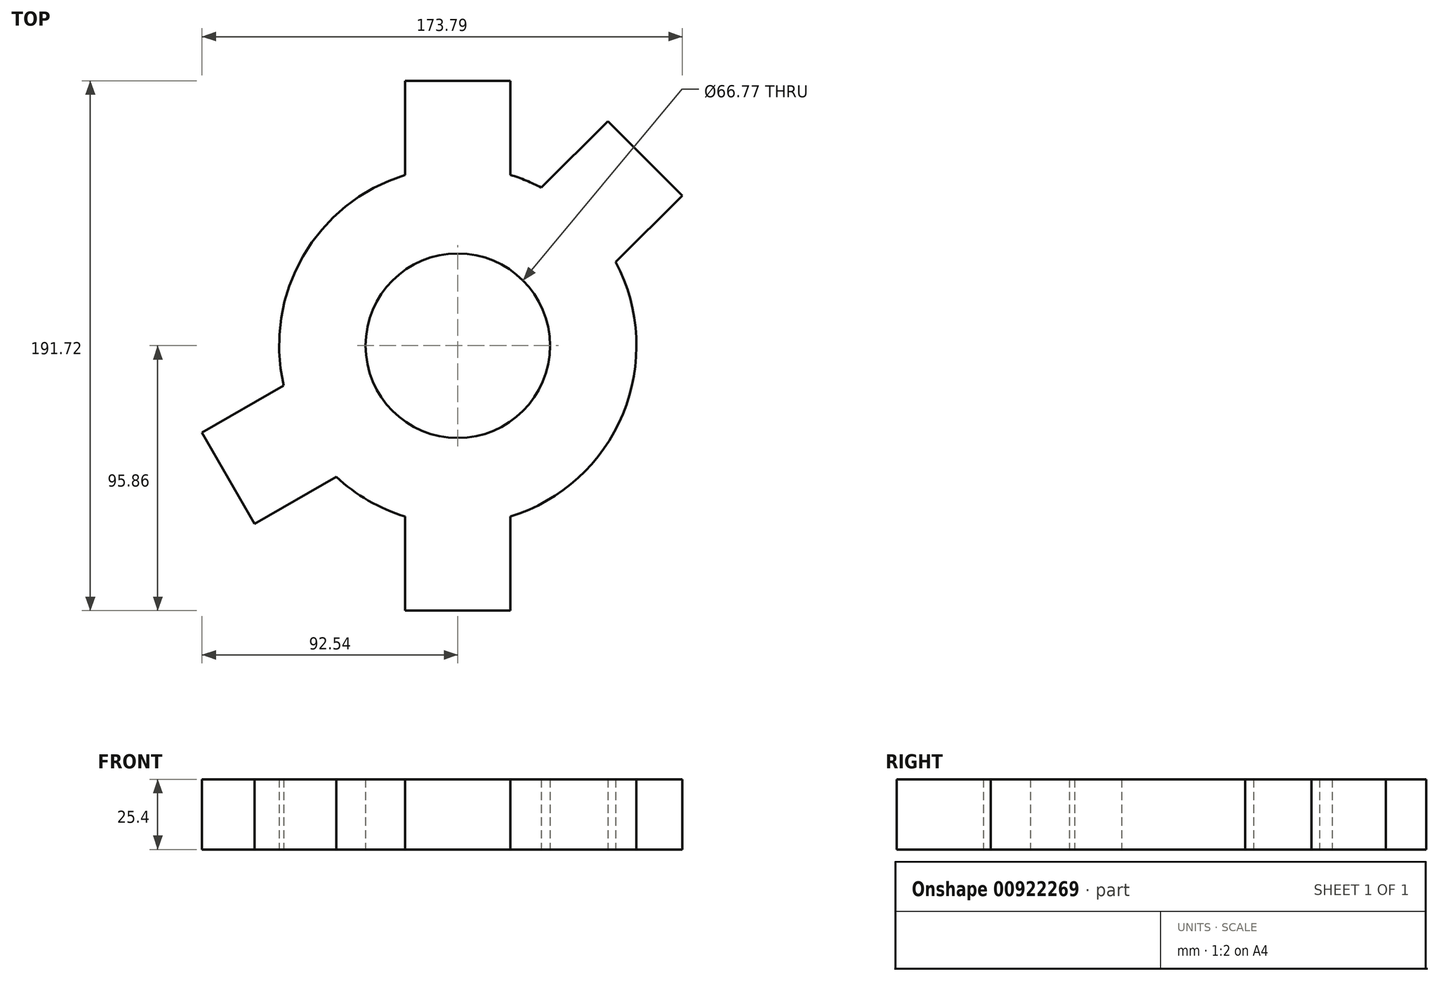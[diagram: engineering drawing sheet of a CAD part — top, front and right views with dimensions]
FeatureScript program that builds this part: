
annotation { "Feature Type Name" : "Feature", "Feature Type Description" : "" }
export const myFeature = defineFeature(function(context is Context, id is Id, definition is map)
    precondition{}
    {
        {
            var Q0;
            Q0=qCreatedBy(makeId("Top.planeOp"),FACE);
            var sketch = newSketch(context, id + "F0", { "sketchPlane" : qUnion([Q0])});
            skCircle(sketch, "E0", {"center": v(0, 0) * mm, "radius": 64.69 * mm});
            skCircle(sketch, "E1", {"center": v(0, 0) * mm, "radius": 33.38 * mm});
            skLineSegment(sketch, "E2", {"start": v(0, 0) * mm, "end": v(0, -64.69) * mm, "construction": true});
            skLineSegment(sketch, "E3", {"start": v(0, 0) * mm, "end": v(45.74, 45.74) * mm, "construction": true});
            skLineSegment(sketch, "E4", {"start": v(0, 0) * mm, "end": v(0, 64.69) * mm, "construction": true});
            skLineSegment(sketch, "E5", {"start": v(0, 0) * mm, "end": v(-56.02, -32.34) * mm, "construction": true});
            skLineSegment(sketch, "E6", {"start": v(19.05, -61.82) * mm, "end": v(19.05, -95.86) * mm});
            skLineSegment(sketch, "E7", {"start": v(30.24, 57.18) * mm, "end": v(54.3, 81.25) * mm});
            skLineSegment(sketch, "E8", {"start": v(19.05, 61.82) * mm, "end": v(19.05, 95.86) * mm});
            skLineSegment(sketch, "E9", {"start": v(-63.06, -14.41) * mm, "end": v(-92.54, -31.43) * mm});
            skLineSegment(sketch, "E10", {"start": v(19.05, -95.86) * mm, "end": v(0, -95.86) * mm});
            skLineSegment(sketch, "E11", {"start": v(54.3, 81.25) * mm, "end": v(67.78, 67.78) * mm});
            skLineSegment(sketch, "E12", {"start": v(19.05, 95.86) * mm, "end": v(0, 95.86) * mm});
            skLineSegment(sketch, "E13", {"start": v(-92.54, -31.43) * mm, "end": v(-83.01, -47.93) * mm});
            skLineSegment(sketch, "E14.MirrorCS", {"start": v(-19.05, -61.82) * mm, "end": v(-19.05, -95.86) * mm});
            skLineSegment(sketch, "E15.MirrorCS", {"start": v(-19.05, -95.86) * mm, "end": v(0, -95.86) * mm});
            skLineSegment(sketch, "E16.MirrorCS", {"start": v(-19.05, 61.82) * mm, "end": v(-19.05, 95.86) * mm});
            skLineSegment(sketch, "E17.MirrorCS", {"start": v(-19.05, 95.86) * mm, "end": v(0, 95.86) * mm});
            skLineSegment(sketch, "E18.MirrorCS", {"start": v(-44.01, -47.4) * mm, "end": v(-73.49, -64.43) * mm});
            skLineSegment(sketch, "E19.MirrorCS", {"start": v(-73.49, -64.43) * mm, "end": v(-83.01, -47.93) * mm});
            skLineSegment(sketch, "E20.MirrorCS", {"start": v(57.18, 30.24) * mm, "end": v(81.25, 54.3) * mm});
            skLineSegment(sketch, "E21.MirrorCS", {"start": v(81.25, 54.3) * mm, "end": v(67.78, 67.78) * mm});
            skSolve(sketch);
        }
        {
            var Q0;
            Q0 = qSketchRegion(id + "F0", true);
            extrude(context, id + "F1", {"entities" : qUnion([Q0]), "depth" : 25.4 * mm, "offsetDistance" : 25.4 * mm});
        }
    });
